# Revit family: _3523240C_ØRSTA FUND.H=1600,CC 240, HE-mast
name_source: partatom
category: Lighting Fixtures
units: mm (PartAtom-declared; Revit-internal decimal feet)

## family parameters
Always vertical = Yes
Cut with Voids When Loaded = No
Light Source = No
Maintain Annotation Orientation = No
OmniClass Number = 23.80.70.14.21
OmniClass Title = Street and Roadway Lighting
Part Type = Normal
Room Calculation Point = No
Round Connector Dimension = Use Diameter
Shared = No
Work Plane-Based = No

## types (1)
- Ørstafundament
    Area = 3,98 m²
    Art.nr = 3523240C
    Art.nr CombiCoat = 3523240C
    CE-godkjent = Ja
    Category = Ørstafundament
    Center of Gravity = X: -0,000 mm Y: -0,000 mm Z: -820,933 mm
    Default Elevation = 0 mm  [stored 0 ft]
    Density = 7860,00 kg/m³
    Description = ØRSTA FUND.H=1600,CC 240, HE-mast
    Design Status = 1
    Designer = khk
    EL nr CombiCoat = 3615522
    Filnamn-VO = Standard
    Filnavn = ØRSTA FUND.H=1600,CC 240, HE-mast
    Fotplate C/C bolter = 240
    Manufacturer = Vik Ørsta AS
    Mass = 47,74 kg
    Materialkvalitet = S355
    Model = _3523240C
    Part Number = 3523240C_BIM
    Requested Accuracy = Low
    Revision Number = -
    Size = 0,0,0
    Sti&Filnamn-VO = Standard
    Title = ØRSTA FUND.H=1600,CC 240, HE-mast
    Volume = 0,01 m³

note: [stored X ft] marks values corroborated as IEEE doubles in the binary element streams (Revit-internal decimal feet)

## geometry (parser evidence)
native form markers: Sweep x2
no freeform markers — native parametric forms only
